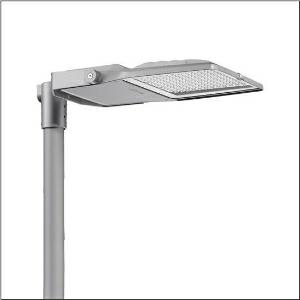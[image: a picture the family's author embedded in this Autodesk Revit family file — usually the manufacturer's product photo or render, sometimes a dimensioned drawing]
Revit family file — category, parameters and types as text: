
# Revit family: floodlight_fl_21_midi___pl61_5xa7781e4c3a_254f
name_source: partatom
category: Lighting Fixtures
units: mm (PartAtom-declared; Revit-internal decimal feet)

## family parameters
Cut with Voids When Loaded = No
Host = Face
Light Source = No
Part Type = Normal
Room Calculation Point = No
Round Connector Dimension = Use Diameter
Shared = No

## types (1)
- --- (1 x LED, 27490 lm, 208.1 W, 4000K)
    Apparent Load = 208 VA
    CIE Flux Codes = 33 65 98 100 100
    Color Rendering = 70
    Color Temperature = 4000K
    Default Elevation = 1800 mm
    Description = Floodlight FL 21 midi, floodlight, primary light control with lens, of PMMA, primary optical cover: protective disc, of toughened safety glass, transparent, light distribution: PL61, light emission: direct distribution, installation type: surface-mounted, LED, High Power LED, rated luminous flux: 27.490lm, luminous efficacy: 132lm/W, light colour: 740, colour temperature: 4000K, control gear: ECG iQ, control: optimised constant luminous flux control (CLO 2.0), Desk-Remote (wireless, voltage-free reading and setting of iQ features in the workshop via application-optimized NFC function/RFID function), Light-Fading, Smart-Wire, Night-Set, Lumen-Switch, Temp-Guard, Auto-Match, with terminal, 6-pole, mains connection: 220..240V, AC, 50/60Hz, start of lifetime: 208W, end of lifetime: 227W, reduction: 90W, luminaire housing, of diecast aluminium, powder-coated, Siteco® metallic grey (DB 702S), corrosivity category C5 according to DIN EN ISO 12944, mast bracket, of steel, galvanised, powder-coated, Siteco® metallic grey (DB 702S), protection rating (complete): IP66, insulation class (complete): insulation class I (protective earthing), certification: CE, protection symbol: D, impact resistance: IK08, permissible operating ambient temperature: -40..+40°C, permissible operating ambient temperature for outdoor applications: -40..+50°C, standard: DIN EN 12944, packaging unit: 1 piece

Light Distribution: PL61
    Height = 76 mm
    Lamp = 1 x LED
    Lamp Light Flux = 27490 lm
    Lamp Power = 208.1 W
    Lamp count = 1
    Length = 657 mm
    Luminous efficacy = 132 lm/W
    Manufacturer = Siteco
    ModVariant = No
    Model = 5XA7781E4C3A
    Number of Poles = 1
    OnlyDefault = Yes
    Power Factor = 1
    Product Name = Floodlight FL 21 midi | PL61
    Product group = floodlight | pylon top
    ProductGroupID = 6101
    Protection Class = Protection class I
    Protection Degree = IP 66
    RLX_Detail_Level = 1
    RlxData = <blob elided: 153313 chars, md5=21baf90c>
    Socket = socket
    Standby Power = 0 W
    System Light Flux = 27490 lm
    System Power = 208 W
    Type Comments = factory setting: luminous flux: 100 % | dim-lin: 254 | 710 mA
    Type Image = l_1007123.jpg
    URL = http://relux.com
    VarID = @adj_017341
    Voltage = 0 V
    Weight = 0.00 kg
    Width = 442 mm

## geometry (parser evidence)
native form markers: Blend x4, Sweep x16
no freeform markers — native parametric forms only
